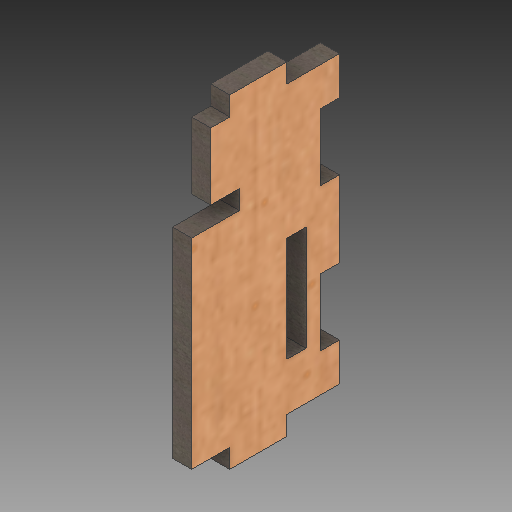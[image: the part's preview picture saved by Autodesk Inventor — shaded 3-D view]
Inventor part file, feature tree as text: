
AUTODESK INVENTOR PART (.ipt)
format: ipt  version: 2019 (Build 230136000, 136)  size: 203,264 bytes
history: native  units: mm
features: other x1, extrude x1, sketch x1
ambient origin geometry x8: Origin, YZ Plane, XZ Plane, XY Plane, X Axis, Y Axis, Z Axis, Center Point
bodies: Body1 (feature_tree)
feature tree (3):
  other  "Твердое тело1"
  extrude  "Выдавливание1"  Depth=4.0mm
  sketch  "Эскиз2"
